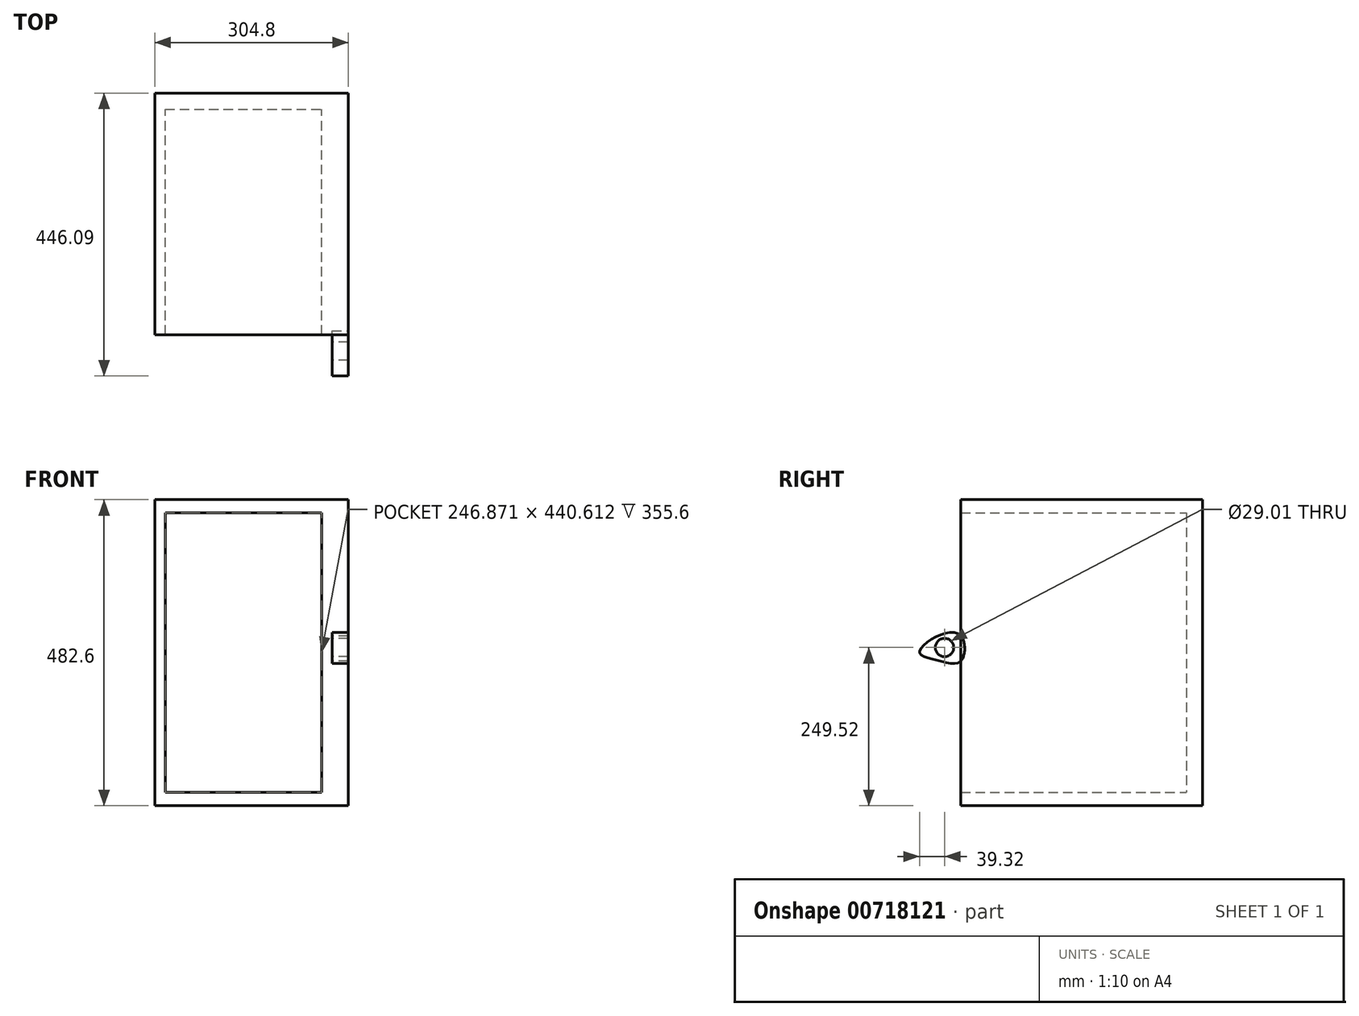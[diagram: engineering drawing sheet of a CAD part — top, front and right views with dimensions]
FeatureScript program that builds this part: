
annotation { "Feature Type Name" : "Feature", "Feature Type Description" : "" }
export const myFeature = defineFeature(function(context is Context, id is Id, definition is map)
    precondition{}
    {
        {
            var Q0;
            Q0=qCreatedBy(makeId("Front.planeOp"),FACE);
            var sketch = newSketch(context, id + "F0", { "sketchPlane" : qUnion([Q0])});
            skLineSegment(sketch, "E0.bottom", {"start": v(-139.7, 241.3) * mm, "end": v(139.7, 241.3) * mm});
            skLineSegment(sketch, "E0.top", {"start": v(-139.7, -241.3) * mm, "end": v(139.7, -241.3) * mm});
            skLineSegment(sketch, "E0.left", {"start": v(-139.7, 241.3) * mm, "end": v(-139.7, -241.3) * mm});
            skLineSegment(sketch, "E0.right", {"start": v(139.7, 241.3) * mm, "end": v(139.7, -241.3) * mm});
            skPoint(sketch, "E0.middle", {"position": v(0, 0) * mm});
            skLineSegment(sketch, "E1.bottom", {"start": v(-123.44, 220.3) * mm, "end": v(123.44, 220.3) * mm});
            skLineSegment(sketch, "E1.top", {"start": v(-123.44, -220.3) * mm, "end": v(123.44, -220.3) * mm});
            skLineSegment(sketch, "E1.left", {"start": v(-123.44, 220.3) * mm, "end": v(-123.44, -220.3) * mm});
            skLineSegment(sketch, "E1.right", {"start": v(123.44, 220.3) * mm, "end": v(123.44, -220.3) * mm});
            skSolve(sketch);
        }
        {
            var Q0;
            Q0 = qSketchRegion(id + "F0", true);
            extrude(context, id + "F1", {"entities" : qUnion([Q0]), "depth" : 381 * mm, "offsetDistance" : 25.4 * mm});
        }
        {
            var Q0;
            Q0=makeQuery(id+"F0.imprint","IMPRINT",FACE,{"disambiguationData":[TD([[makeQuery(id+"F0.imprint","IMPRINT",EDGE,{"derivedFrom":sQuery(id+"F0.wireOp",EDGE,"E1.bottom")}),-1.0]])]});
            extrude(context, id + "F2", {"entities" : qUnion([Q0]), "operationType" : NewBodyOperationType.ADD, "depth" : 25.4 * mm, "offsetDistance" : 25.4 * mm});
        }
        {
            var Q0;
            Q0=makeQuery(id+"F1.opExtrude","SWEPT_FACE",FACE,{"disambiguationData":[OSD([sQuery(id+"F0.wireOp",EDGE,"E0.right")])]});
            var sketch = newSketch(context, id + "F3", { "sketchPlane" : qUnion([Q0])});
            skFitSpline(sketch, "E2", {"points": [v(-381, 26.6) * mm, v(-421.34, 24.66) * mm, v(-445.96, 0) * mm, v(-417.24, -12.09) * mm, v(-381, -13.06) * mm, v(-381, 26.6) * mm]});
            skCircle(sketch, "E3", {"center": v(-406.77, 8.22) * mm, "radius": 14.5 * mm});
            skSolve(sketch);
        }
        {
            var Q0;
            Q0=makeQuery(id+"F3.imprint","IMPRINT",FACE,{"disambiguationData":[TD([[makeQuery(id+"F3.imprint","IMPRINT",EDGE,{"derivedFrom":sQuery(id+"F3.wireOp",EDGE,"E3")}),-1.0]])]});
            var Q1;
            {var subQ0=sQuery(id+"F0.wireOp",EDGE,"E0.right");Q1=makeQuery(id+"F3.imprint","IMPRINT",FACE,{"disambiguationData":[TD([[makeQuery(id+"F3.imprint","IMPRINT",EDGE,{"derivedFrom":makeQuery(id+"F1.opExtrude","CAP_EDGE",EDGE,{"disambiguationData":[OSD([subQ0])],"isStart":true})}),-1.0]])]});}
            extrude(context, id + "F4", {"entities" : qUnion([Q0, Q1]), "operationType" : NewBodyOperationType.ADD, "depth" : 25.4 * mm, "offsetDistance" : 25.4 * mm});
        }
    });
